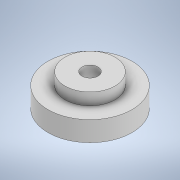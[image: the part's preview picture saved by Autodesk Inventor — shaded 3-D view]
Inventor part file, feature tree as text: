
AUTODESK INVENTOR PART (.ipt)
format: ipt  version: 2021 (Build 250183000, 183)  size: 110,080 bytes
history: native  units: mm
features: extrude x2, sketch x2
ambient origin geometry x8: Origin, YZ Plane, XZ Plane, XY Plane, X Axis, Y Axis, Z Axis, Center Point
bodies: Solid1 (feature_tree)
feature tree (4):
  extrude  "Extrusion1"  Depth=8.0mm
  extrude  "Extrusion2"  Depth=6.0mm
  sketch  "Sketch1"  dims[d0=42.0mm d1=8.0mm]
  sketch  "Sketch2"  dims[d2=10.0mm d3=0.0mm d4=8.0mm d5=25.0mm d6=6.0mm d7=0.0mm]
